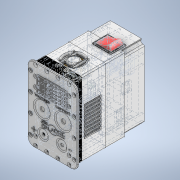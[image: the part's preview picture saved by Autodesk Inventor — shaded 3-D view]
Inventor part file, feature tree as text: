
AUTODESK INVENTOR PART (.ipt)
format: ipt  version: 2022 (Build 260153000, 153)  size: 3,496,960 bytes
history: native  units: in
note: dims shown in document units (in); Inventor stores cm internally (conversion verified against a paired STEP export)
features: sketch x46, extrude x43, fillet x26, other x15, hole x5, chamfer x3, plane x1, split x1
ambient origin geometry x8: Origin, YZ Plane, XZ Plane, XY Plane, X Axis, Y Axis, Z Axis, Center Point
bodies: Body1 (feature_tree), Body2 (feature_tree), Body3 (feature_tree), Body4 (feature_tree), Body5 (feature_tree), Body6 (feature_tree), Body7 (feature_tree), Body8 (feature_tree), Body9 (feature_tree), Body10 (feature_tree), Body11 (feature_tree), Body12 (feature_tree), Body13 (feature_tree)
feature tree (140):
  other  "Faceplate"
  extrude  "Front Panel Blank"  Depth=4.7244in
  hole  "Panel Mount Screw Holes"  [1 undecoded]
  extrude  "Voltmeter Screen"  Depth=0.0984in TaperAngle=0.0deg
  extrude  "Knob Indents"  Depth=0.1181in
  extrude  "Pot Mounting Holes"  Depth=0.1181in
  extrude  "Connector Indents"  Depth=0.1181in
  extrude  "Connector Mounting Holes"  Depth=0.5906in
  fillet  "Fillet1"  Radius=0.5906in
  other  "Work Point1"
  extrude  "Pot Back Keepouts"  Depth=1.1811in
  extrude  "Chassis"  Depth=0.5906in
  extrude  "Display"  Depth=0.1969in
  extrude  "Chassis 2"  Depth=1.7717in
  extrude  "Back Chassis Plate"  Depth=0.4724in
  extrude  "PCB Standoffs"  Depth=0.0197in
  extrude  "PCB"  Depth=0.0197in
  hole  "PCB Screw Mounts"  [1 undecoded]
  extrude  "Heatsinks"  Depth=1.063in
  extrude  "Air Holes 1"  Depth=0.7874in
  fillet  "Fillet2"  Radius=0.9449in
  fillet  "Fillet3"  Radius=0.7874in
  extrude  "Fan Body"  Depth=0.6693in
  extrude  "Top Air Holes"  Depth=0.2756in
  hole  "Hole5"  [1 undecoded]
  fillet  "Fillet11"  Radius=0.5512in
  fillet  "Fillet12"  Radius=0.5512in
  fillet  "Fillet13"  Radius=1.378in
  fillet  "Fillet14"  Radius=0.5906in
  extrude  "Text Labels"  Depth=0.0394in
  extrude  "Logo"  TaperAngle=0.0deg  [1 undecoded]
  fillet  "Fillet15"  Radius=0.5906in
  fillet  "Fillet16"  Radius=0.0787in
  fillet  "Fillet17"  Radius=2.3622in
  fillet  "Fillet18"  Radius=1.1811in
  fillet  "Fillet19"  Radius=0.3937in
  fillet  "Fillet20"  Radius=0.5906in
  fillet  "Fillet21"  Radius=1.9685in
  fillet  "Fillet24"  Radius=0.1181in
  fillet  "Fillet25"  Radius=0.1181in
  fillet  "Fillet26"  Radius=0.1181in
  extrude  "Body 3 Mains Section"  Depth=0.1181in
  extrude  "Transformer Metal"  Depth=0.2362in
  extrude  "Transformer Yellow"  Depth=0.1476in
  extrude  "body3 lid"  Depth=0.2756in
  extrude  "IEC Panelmount"  Depth=0.3346in
  extrude  "IEC inside"  Depth=0.3346in
  extrude  "IEC socket"  Depth=0.3346in
  extrude  "body3 IEC hole"  Depth=0.7087in
  chamfer  "IEPin Sculpting"  Distance=0.3937in
  fillet  "Fillet27"  Radius=0.2756in
  fillet  "Fillet28"  Radius=0.315in
  fillet  "Fillet29"  Radius=0.1181in
  hole  "IEC Screwholes"  [1 undecoded]
  hole  "Faceplate Mounting Holes"  [1 undecoded]
  sketch  "Sketch41"  dims[d153=0.7087in d154=0.7087in]
  extrude  "IEC Pins"  Depth=0.2362in
  chamfer  "Chamfer2"  Distance=0.1181in
  extrude  "Switch Panel Mount"  Depth=0.5906in
  extrude  "Switch Body"  Depth=0.6299in
  extrude  "Switch Switch"  Depth=0.0787in TaperAngle=0.0deg
  extrude  "Switch Carve"  Depth=1.378in TaperAngle=0.0deg
  fillet  "Fillet30"  Radius=0.1181in
  fillet  "Fillet31"  Radius=0.3543in
  extrude  "Extrusion34"  Depth=0.3543in
  chamfer  "Chamfer3"  Distance=0.3543in
  extrude  "Extrusion35"  Depth=0.3543in
  extrude  "Extrusion36"  Depth=1.0236in
  fillet  "Fillet32"  Radius=2.3031in
  extrude  "Extrusion37"  Depth=0.0512in
  extrude  "Extrusion38"  Depth=0.1969in TaperAngle=0.0deg
  extrude  "Extrusion39"  Depth=0.0512in
  extrude  "Extrusion40"  Depth=1.4567in
  fillet  "Fillet33"  Radius=0.128in
  plane  "Work Plane1"
  split  "Split1"
  extrude  "Extrusion41"  Depth=0.0512in
  extrude  "Extrusion42"  Depth=0.0512in
  fillet  "Fillet34"  Radius=0.063in
  extrude  "Extrusion43"  Depth=0.0512in
  extrude  "Extrusion44"  Depth=0.0512in
  fillet  "Fillet35"  Radius=0.1181in
  sketch  "Sketch1"  dims[d0=3.1496in d1=4.7244in]
  sketch  "Sketch2"  dims[d2=2.3622in d4=1.5748in]
  sketch  "Sketch3"  dims[d5=0.3937in d6=0.0984in d7=0.0in]
  sketch  "Sketch4"  dims[d8=0.1181in d9=0.1181in]
  sketch  "Sketch5"  dims[d10=0.1181in d11=0.1181in]
  sketch  "Sketch6"  dims[d12=0.1181in d13=0.1181in]
  sketch  "Sketch7"  dims[d14=0.1181in d15=0.1181in d16=0.5906in]
  other  "Body 1"
  sketch  "Sketch11"  dims[d17=0.5906in d18=1.1811in]
  sketch  "Sketch14"  dims[d19=0.5906in d20=0.5906in]
  other  "Pots"
  sketch  "Sketch15"  dims[d21=0.1969in d22=0.1969in]
  other  "Screen"
  sketch  "Sketch16"  dims[d23=0.126in d24=0.2362in d25=0.248in d26=0.0787in d27=90.0deg d28=0.315in d29=0.8108in d30=1.7717in]
  other  "Body 2"
  sketch  "Sketch17"  dims[d31=0.5906in d32=1.0236in d33=0.8858in d34=0.9449in d35=0.4724in]
  sketch  "Sketch18"  dims[d36=0.0197in d37=0.0197in d38=0.0197in]
  other  "Power Module"
  sketch  "Sketch20"  dims[d39=0.0197in d40=0.9449in]
  sketch  "Sketch21"  dims[d42=0.5906in d43=1.0236in]
  other  "Power Moudle Heat Sinks"
  sketch  "Sketch22"  dims[d44=0.4724in d45=1.063in]
  sketch  "Sketch24"  dims[d46=0.1969in d47=0.0in d48=0.9449in d49=0.9449in d50=0.7874in]
  other  "Cooling_fan"
  sketch  "Sketch25"  dims[d51=0.6693in d52=0.6693in]
  sketch  "Sketch26"  dims[d53=0.0394in d54=0.0in d55=0.2756in]
  sketch  "Sketch28"  dims[d56=0.2756in d57=0.0394in d58=0.0in d59=0.5512in d60=0.5512in d61=1.378in d64=0.5906in]
  sketch  "Sketch30"  dims[d65=0.0394in d66=0.0in d67=0.187in]
  other  "Body 3"
  sketch  "Sketch31"  dims[d68=0.187in d69=0.0in d70=0.0in d71=0.5906in d72=0.0787in d81=2.3622in d82=1.1811in d85=0.3937in d86=0.2756in d87=0.5906in d88=0.0in d91=1.9685in d99=0.1181in d100=0.1181in d101=0.1181in]
  other  "Transformer"
  sketch  "Sketch32"  dims[d102=0.1181in d103=0.1181in]
  sketch  "Sketch33"  dims[d104=0.2362in d105=0.2362in]
  sketch  "Sketch34"  dims[d106=0.1181in d109=0.1476in]
  other  "IEC"
  sketch  "Sketch35"  dims[d110=0.2756in d111=0.128in]
  sketch  "Sketch36"  dims[d147=0.6693in d148=0.3346in]
  sketch  "Sketch37"  dims[d149=0.6693in d150=0.3346in]
  sketch  "Sketch39"  dims[d151=0.3346in d152=0.3346in]
  sketch  "Sketch42"  dims[d155=0.748in]
  sketch  "Sketch43"  dims[d156=0.748in d157=0.3937in d158=0.0in d160=0.2756in d161=0.315in d164=0.1181in]
  other  "Power Switch"
  sketch  "Sketch44"  dims[d165=1.1811in d166=0.1181in]
  sketch  "Sketch45"  dims[d167=0.315in d168=0.315in]
  sketch  "Sketch46"  dims[d169=0.2362in d170=0.2362in]
  sketch  "Sketch47"  dims[d171=2.7559in]
  sketch  "Sketch48"  dims[d172=1.1811in]
  sketch  "Sketch49"  dims[d173=0.6693in]
  sketch  "Sketch50"  dims[d174=0.2756in]
  sketch  "Sketch51"  dims[d175=0.1181in]
  sketch  "Sketch52"  dims[d176=0.1181in]
  sketch  "Sketch53"  dims[d177=0.1181in]
  sketch  "Sketch54"  dims[d178=0.1181in]
  sketch  "Sketch55"  dims[d179=0.1181in]
  sketch  "Sketch57"  dims[d180=0.1181in]
  sketch  "Sketch58"  dims[d181=0.1181in d182=0.1181in d183=0.1476in d185=0.5906in d186=0.6299in d187=0.0968in d188=0.2362in d189=0.248in d190=0.0787in d191=90.0deg d192=1.4961in d193=0.8108in d194=0.0787in d195=0.6693in d196=0.0in d197=0.0in d216=1.378in d217=0.0in d218=0.1181in d219=0.0in d220=0.3543in d221=0.3543in d222=0.3543in d223=0.3543in d224=1.0236in d225=2.3031in d226=0.5118in d230=0.1969in d231=0.0in d232=2.5591in d233=1.4567in d234=0.128in d235=0.0886in d236=0.7283in d237=0.063in d238=0.0in d239=0.1181in d240=0.1181in d241=0.1181in d242=0.1181in d243=0.0968in d244=0.2362in d245=0.248in d246=0.0787in d247=90.0deg d248=0.315in d249=0.8108in d250=0.0394in d251=0.1575in d252=0.1575in d253=0.0394in d254=0.0394in d255=0.1575in d256=0.0394in d257=0.1575in d258=0.0394in d259=0.1575in d260=0.0394in d261=0.1575in d262=0.0394in d263=0.1575in d264=0.0394in d265=0.1575in d266=0.0394in d267=0.1575in d268=0.0394in d269=1.811in d270=0.0906in d271=0.3937in d272=0.0906in d274=0.374in d275=0.374in d276=0.8268in d277=0.0in d278=0.1969in d288=1.9685in d289=1.5748in d290=1.1811in d295=0.6693in d296=1.122in d304=0.0984in d305=0.0984in d306=0.0984in d307=0.0984in d308=0.0984in d309=0.0984in d310=0.0984in d311=0.0984in d312=0.0984in d313=0.1181in d314=0.1181in d315=0.1181in d316=0.1181in d317=0.1181in d318=0.1181in d319=0.1181in d320=0.1181in d321=0.315in d322=0.1969in d323=0.0in d324=0.0in d326=0.0689in d327=0.0689in d353=0.3937in d354=0.0in d355=0.0394in d356=0.0787in d357=1.1811in d358=1.1811in d359=0.0787in d360=0.0787in d361=0.0787in d362=0.0787in d363=0.9449in d364=0.9449in d365=0.1181in d366=0.1181in d367=0.1181in d368=0.1181in d375=0.5512in d376=0.0in d377=1.1024in d378=0.5906in d379=0.5906in d380=0.7283in d381=0.0787in d382=0.0787in d383=0.0787in d384=0.0394in d385=0.0394in d386=0.0394in d387=0.0787in d388=0.0787in d389=0.3642in d390=0.5512in d391=0.3642in d392=0.5512in d393=0.3642in d394=0.5512in d395=0.3642in d396=0.5512in d397=0.0787in d398=0.0787in d399=0.0408in d400=0.1877in d401=0.0408in d402=0.0408in d403=0.5906in d404=0.5906in d405=0.0787in d406=0.1181in d441=0.0787in d442=0.0787in d443=0.0787in d444=0.0787in d445=0.0617in d446=0.1575in d447=0.119in d448=0.188in d449=0.5635in d450=0.248in d451=0.0in d452=0.0787in d453=0.0787in d454=0.0394in d455=0.0394in d456=0.1181in d457=0.1181in d459=0.5118in d460=0.2362in d461=0.7087in d463=0.7087in d464=0.7087in d465=0.0787in d466=0.0787in d468=0.4134in d471=1.3386in d472=0.1969in d473=0.5709in d476=0.0787in d477=0.0in d479=0.0787in d480=0.0in d481=0.0in d488=0.0in d489=0.0in d490=0.7382in d491=0.1772in d492=0.1772in d493=0.7382in d494=0.1772in d495=0.1772in d496=0.1772in d497=0.1772in d498=0.5512in d499=0.5512in d500=0.5512in d501=0.6693in d502=0.3642in d503=0.3642in d504=0.187in d505=0.187in d506=0.0984in d507=0.0984in d508=0.0787in d509=0.0787in d510=0.0787in d511=0.0394in d512=0.0118in d513=4.7244in d514=2.3622in d515=0.0in d518=0.0551in d519=0.0551in d520=0.0551in d521=1.5945in d532=0.5512in d533=1.2205in d534=1.8976in d535=0.0in d536=1.2598in d537=1.1417in d538=0.2264in d539=0.2264in d540=0.3189in d541=0.3189in d542=0.5118in d543=1.6614in d544=0.0in d545=0.0in d546=0.1181in d547=0.0in d549=1.3012in d552=0.6506in d553=1.124in d554=0.3268in d555=0.6506in d556=0.6506in d557=0.3268in d558=0.1969in d559=0.0in d560=1.2205in d561=1.063in d562=0.0394in d564=0.0305in d566=0.5512in d567=0.9843in d568=0.9843in d570=0.2559in d571=0.2362in d572=0.0305in d573=0.2559in d574=0.689in d575=0.0in d576=0.9567in d577=0.6535in d578=0.1205in d579=0.0837in d580=0.0837in d581=0.5402in d582=0.2083in d583=0.2083in d585=0.1969in d586=0.0787in d587=0.0787in d588=0.0787in d589=0.1575in d590=0.1575in d591=0.1575in d592=0.1575in d593=0.3307in d594=0.439in d595=0.439in d596=0.1575in d597=0.1575in d598=0.689in d599=0.0in d600=0.689in d601=0.0in d602=0.0394in d603=0.0787in d604=45.0deg d605=0.1969in d606=0.1181in d607=0.1181in d608=0.2247in d609=0.2247in d611=1.437in d612=0.2402in d613=0.2402in d614=0.6496in d615=0.0968in d616=0.2362in d617=0.1575in d618=0.0787in d619=90.0deg d620=0.315in d621=0.8108in d622=0.9449in d623=0.0394in d624=1.7776in d625=0.3268in d631=1.6772in d632=1.6772in d633=1.1417in d634=1.0236in d638=0.063in d639=0.063in d640=0.063in d641=0.0787in d642=0.1181in d643=0.3937in d644=0.2559in d645=0.2559in d646=0.2559in d647=0.1693in d648=0.5906in d649=1.1024in d650=0.4724in d651=0.0in d652=0.0197in d653=0.0787in d654=45.0deg d655=0.2756in d656=0.2756in d657=0.2362in d658=0.2362in d659=0.1476in d660=0.1476in d661=1.1811in d662=0.9843in d663=0.0787in d664=0.0in d665=0.8528in d666=1.0669in d667=0.0571in d668=0.0571in d669=0.0657in d670=0.0657in d671=0.7087in d672=0.0in d673=0.1063in d674=0.1063in d675=0.1063in d676=0.1063in d677=0.2756in d678=0.0in d679=0.1575in d680=0.0394in d681=1.378in d682=0.3937in d683=0.0079in d684=0.2756in d685=0.0in d686=0.0197in d687=0.0118in d688=0.0394in d689=0.2953in d690=0.0394in d691=0.1181in d692=0.8528in d693=0.4264in d694=0.315in d695=0.4067in d696=0.4067in d697=0.0315in d698=0.0315in d699=0.248in d700=0.248in d701=0.1732in d702=0.1772in d704=0.0787in d705=0.0787in d706=0.0591in d707=0.0591in d708=0.0591in d709=0.0591in d710=0.0394in d711=0.0394in d712=0.0394in d713=0.0394in d714=0.2953in d715=0.4067in d716=0.1732in d717=0.1772in d718=0.0787in d719=0.0787in d720=0.4331in d721=0.0in d722=0.0394in d723=0.0787in d724=45.0deg d725=0.4331in d726=0.0in d727=0.0591in d728=0.0591in d729=0.0591in d730=0.0591in d731=0.1969in d732=0.0in d733=0.0787in d734=0.0in d735=0.1969in d736=0.0in d737=0.0in d738=0.5512in d739=0.5906in d740=0.1181in d741=0.1181in d742=0.1181in d743=0.1181in d744=0.0in d745=0.0in d746=0.2165in d747=0.2165in d748=0.2165in d749=0.2165in d750=1.2598in d751=0.0in d752=0.1181in d753=0.1181in d754=0.3937in d755=0.3937in d756=0.1181in d757=0.1181in d758=1.2598in d759=0.0in d760=0.0787in d764=0.3937in d765=0.3937in d766=0.1181in d767=0.1181in d768=0.1181in d769=0.1181in d770=0.0669in d771=0.0669in d772=0.1024in d773=0.5906in d774=0.3937in d775=1.5748in d776=0.5906in d777=0.0669in d778=0.0669in d779=0.3937in d780=0.0in d781=0.4724in d782=0.0in d783=0.0512in d784=0.063in d786=0.063in d788=0.0079in d789=0.063in d790=0.063in d791=0.0079in d792=0.0079in d793=0.0079in d794=0.063in d795=0.063in d796=0.063in d797=0.063in d798=0.4724in d799=0.0in d800=0.5906in d801=0.3937in d802=0.0669in d803=0.0669in d804=0.0669in d805=0.0669in d806=0.5906in d807=2.1654in d808=0.3937in d809=0.0in d810=0.0512in]
  other  "Body 3 A"
  other  "Body 3 B"
note: 6 required parameter values undecoded (feature->parameter linkage not recoverable at this tier; creation-order binding heuristic only, values carry confidence <= 0.55)
